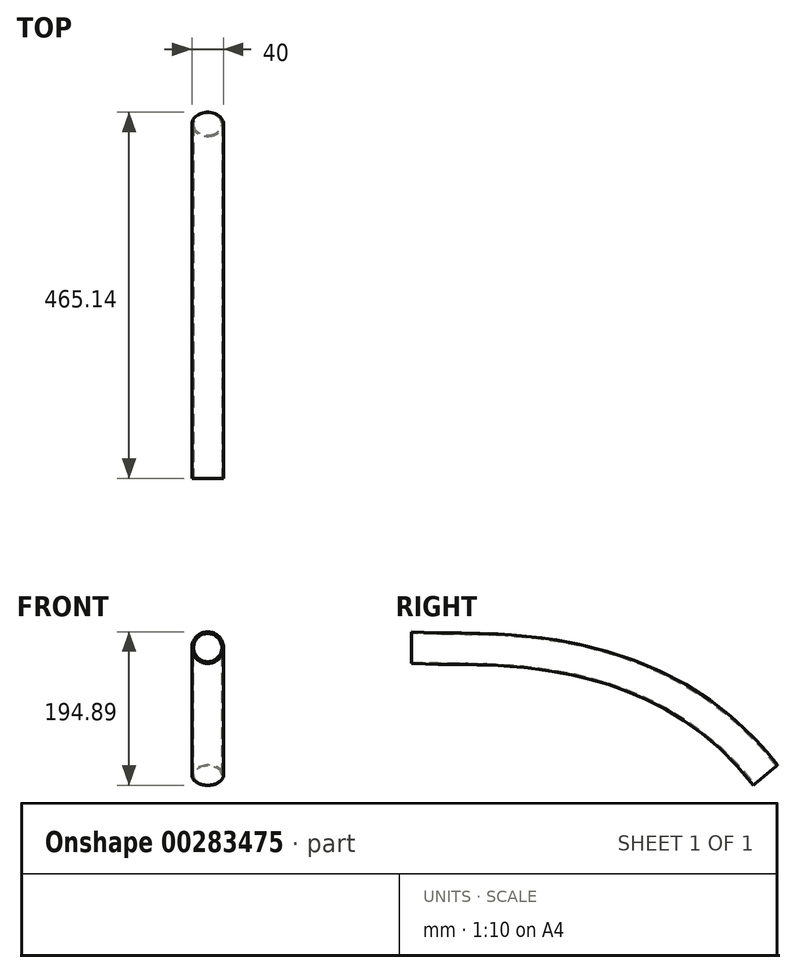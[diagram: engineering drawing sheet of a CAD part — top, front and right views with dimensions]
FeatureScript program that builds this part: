
annotation { "Feature Type Name" : "Feature", "Feature Type Description" : "" }
export const myFeature = defineFeature(function(context is Context, id is Id, definition is map)
    precondition{}
    {
        {
            var Q0;
            Q0=qCreatedBy(makeId("Right.planeOp"),FACE);
            var sketch = newSketch(context, id + "F0", { "sketchPlane" : qUnion([Q0])});
            skPoint(sketch, "E0", {"position": v(0, 0) * mm});
            skPoint(sketch, "E1", {"position": v(449.82, 0) * mm});
            skPoint(sketch, "E2", {"position": v(449.82, -162.03) * mm});
            skFitSpline(sketch, "E3", {"points": [v(0, 0) * mm, v(112.23, -2.92) * mm, v(449.82, -162.03) * mm], "startDerivative": vector(451.23, -19.15) * mm, "endDerivative": vector(491.81, -639.07) * mm});
            skSolve(sketch);
        }
        {
            var Q0;
            Q0=qCreatedBy(makeId("Front.planeOp"),FACE);
            var sketch = newSketch(context, id + "F1", { "sketchPlane" : qUnion([Q0])});
            skPoint(sketch, "E4.0", {"position": v(0, 0) * mm});
            skCircle(sketch, "E5", {"center": v(0, 0) * mm, "radius": 20 * mm});
            skCircle(sketch, "E6.0", {"center": v(0, 0) * mm, "radius": 18 * mm});
            skSolve(sketch);
        }
        {
            var Q0;
            Q0=makeQuery(id+"F1.imprint","IMPRINT",FACE,{"disambiguationData":[TD([[makeQuery(id+"F1.imprint","IMPRINT",EDGE,{"derivedFrom":sQuery(id+"F1.wireOp",EDGE,"E5")}),1.0]])]});
            var Q1;
            Q1=sQuery(id+"F0.wireOp",EDGE,"E3");
            sweep(context, id + "F2", {"profiles" : qUnion([Q0]), "path" : qUnion([Q1])});
        }
    });
